# Revit family: CMU-2 Core-Side
name_source: partatom
category: Detail Items
revit_build: Autodesk Revit Architecture 2012 (Build: 20110210_1515)
units: mm (PartAtom-declared; Revit-internal decimal feet)

## types (13) — shared parameters
Joint = 0' - 0 3/8"

## per-type parameters (varying)
| type | Face | Height | Keynote | Length | Thickness | Web |
| 4" x 8" x 16" | 0' - 0 3/4" | 0' - 7 5/8" | 04 22 00.A14 | 1' - 3 5/8" | 0' - 3 5/8" | 0' - 0 3/4" |
| 4" x  8" x 8" | 0' - 0 3/4" | 0' - 7 5/8" | 04 22 00.A2 | 0' - 7 5/8" | 0' - 3 5/8" | 0' - 0 3/4" |
| 8" x 8" x 16" | 0' - 1 1/4" | 0' - 7 5/8" | 04 22 00.A16 | 1' - 3 5/8" | 0' - 7 5/8" | 0' - 1" |
| 8" x 8" x 8" | 0' - 1 1/4" | 0' - 7 5/8" | 04 22 00.A4 | 0' - 7 5/8" | 0' - 7 5/8" | 0' - 1" |
| 2" x 8" x 8" | 0' - 0 1/2" | 0' - 7 5/8" | 04 22 00.A1 | 0' - 7 5/8" | 0' - 1 5/8" | 0' - 0 3/4" |
| 6" x 8" x 8" | 0' - 1" | 0' - 7 5/8" | 04 22 00.A3 | 0' - 7 5/8" | 0' - 5 5/8" | 0' - 1" |
| 4" x 4" x 16" | 0' - 0 3/4" | 0' - 3 5/8" | 04 22 00.A10 | 1' - 3 5/8" | 0' - 3 5/8" | 0' - 0 3/4" |
| 6" x 4" x 16" | 0' - 1" | 0' - 3 5/8" | 04 22 00.A11 | 1' - 3 5/8" | 0' - 5 5/8" | 0' - 1" |
| 8" x 4" x 16" | 0' - 1 1/4" | 0' - 3 5/8" | 04 22 00.A12 | 1' - 3 5/8" | 0' - 7 5/8" | 0' - 1" |
| 2" x 8" x 16" | 0' - 0 1/2" | 0' - 7 5/8" | 04 22 00.A13 | 1' - 3 5/8" | 0' - 1 5/8" | 0' - 0 3/4" |
| 6" x 8" x 16" | 0' - 1" | 0' - 7 5/8" | 04 22 00.A15 | 1' - 3 5/8" | 0' - 5 5/8" | 0' - 1" |
| 10" x 8" x 16" | 0' - 1 3/8" | 0' - 7 5/8" | 04 22 00.A17 | 1' - 3 5/8" | 0' - 9 5/8" | 0' - 1 1/8" |
| 12" x 8" x 16" | 0' - 1 1/2" | 0' - 7 5/8" | 04 22 00.A18 | 1' - 3 5/8" | 0' - 11 5/8" | 0' - 1 1/8" |

## geometry (parser evidence)
native form markers: Sweep x1
no freeform markers — native parametric forms only
